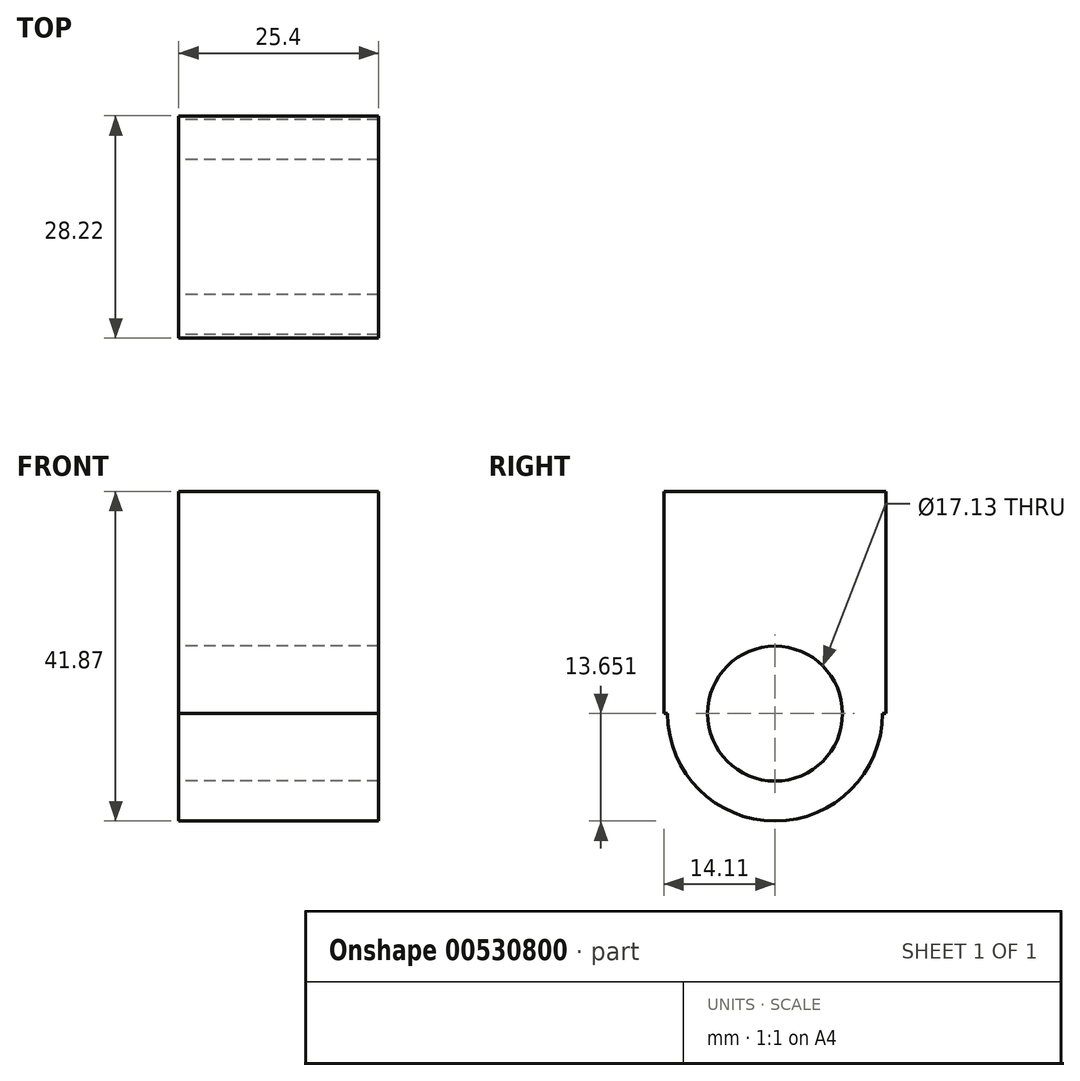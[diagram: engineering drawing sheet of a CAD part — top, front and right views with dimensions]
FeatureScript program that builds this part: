
annotation { "Feature Type Name" : "Feature", "Feature Type Description" : "" }
export const myFeature = defineFeature(function(context is Context, id is Id, definition is map)
    precondition{}
    {
        {
            var Q0;
            Q0=qCreatedBy(makeId("Right.planeOp"),FACE);
            var sketch = newSketch(context, id + "F0", { "sketchPlane" : qUnion([Q0])});
            skLineSegment(sketch, "E0.bottom", {"start": v(14.1, 14.1) * mm, "end": v(-14.1, 14.1) * mm});
            skLineSegment(sketch, "E0.top", {"start": v(14.1, -14.1) * mm, "end": v(13.65, -14.1) * mm});
            skLineSegment(sketch, "E0.left", {"start": v(14.1, 14.1) * mm, "end": v(14.1, -14.1) * mm});
            skLineSegment(sketch, "E0.right", {"start": v(-14.1, 14.1) * mm, "end": v(-14.1, -14.1) * mm});
            skPoint(sketch, "E0.middle", {"position": v(0, 0) * mm});
            skCircle(sketch, "E1", {"center": v(0, -14.1) * mm, "radius": 13.65 * mm});
            skLineSegment(sketch, "E2.trimOffspring", {"start": v(-13.65, -14.1) * mm, "end": v(-14.1, -14.1) * mm});
            skCircle(sketch, "E3.0", {"center": v(0, -14.1) * mm, "radius": 8.57 * mm});
            skSolve(sketch);
        }
        {
            var Q0;
            Q0=makeQuery(id+"F0.imprint","IMPRINT",FACE,{"disambiguationData":[TD([[makeQuery(id+"F0.imprint","IMPRINT",EDGE,{"derivedFrom":sQuery(id+"F0.wireOp",EDGE,"E3.0")}),-1.0]])]});
            var Q1;
            Q1=makeQuery(id+"F0.imprint","IMPRINT",FACE,{"disambiguationData":[TD([[makeQuery(id+"F0.imprint","IMPRINT",EDGE,{"derivedFrom":sQuery(id+"F0.wireOp",EDGE,"E0.bottom")}),1.0]])]});
            extrude(context, id + "F1", {"entities" : qUnion([Q0, Q1]), "depth" : 25.4 * mm});
        }
    });
